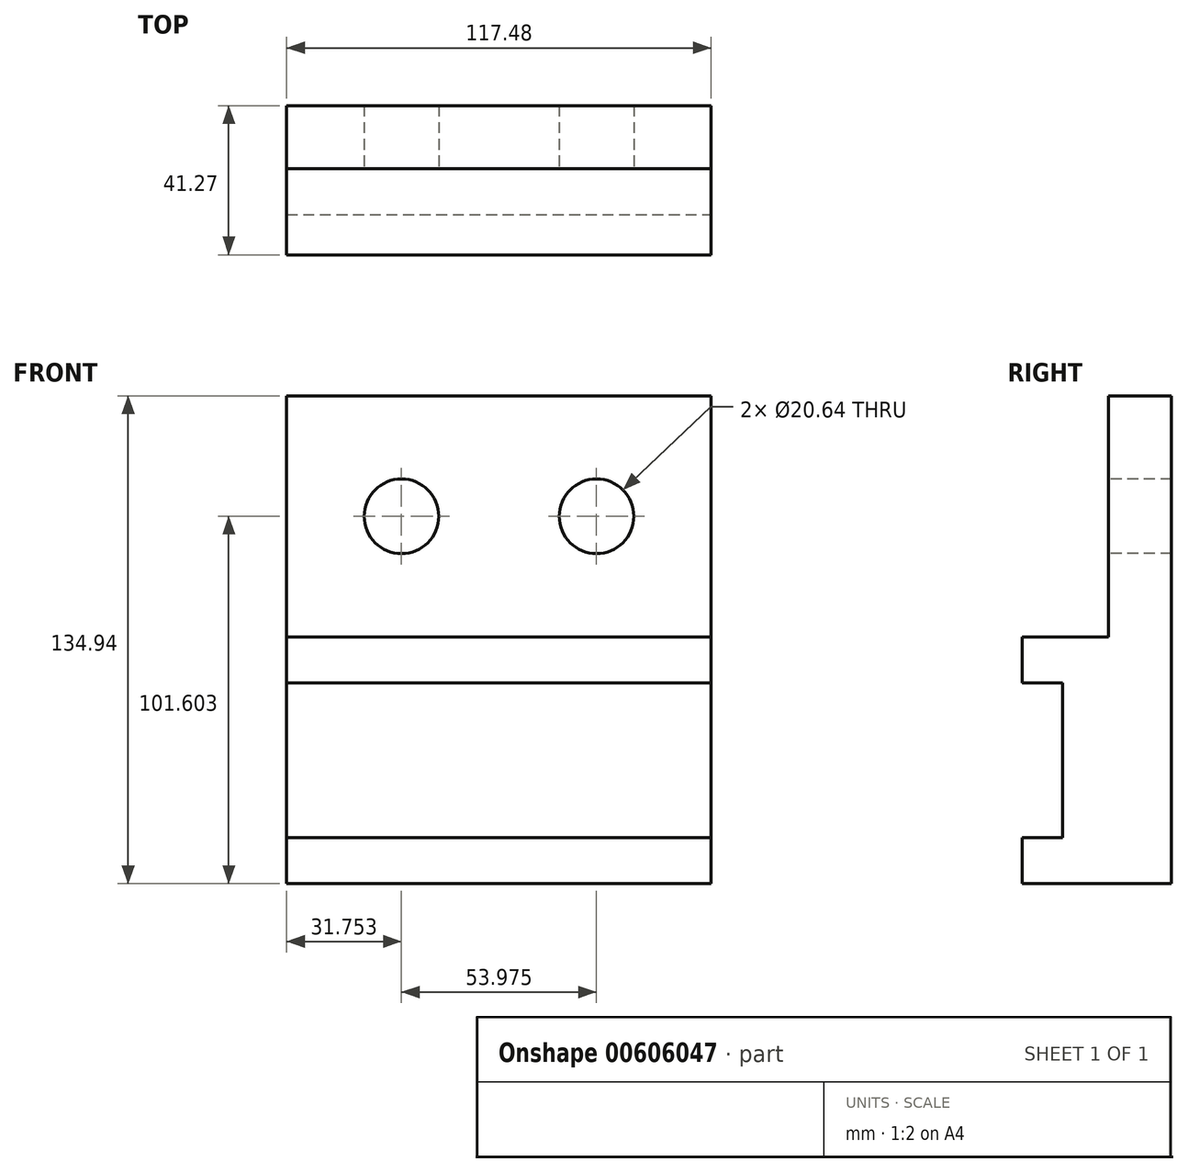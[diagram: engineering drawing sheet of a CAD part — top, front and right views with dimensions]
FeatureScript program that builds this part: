
annotation { "Feature Type Name" : "Feature", "Feature Type Description" : "" }
export const myFeature = defineFeature(function(context is Context, id is Id, definition is map)
    precondition{}
    {
        {
            var Q0;
            Q0=qCreatedBy(makeId("Front.planeOp"),FACE);
            var sketch = newSketch(context, id + "F0", { "sketchPlane" : qUnion([Q0])});
            skLineSegment(sketch, "E0.bottom", {"start": v(-57.2, 10.6) * mm, "end": v(60.27, 10.6) * mm});
            skLineSegment(sketch, "E0.top", {"start": v(-57.2, -57.67) * mm, "end": v(60.27, -57.67) * mm});
            skLineSegment(sketch, "E0.left", {"start": v(-57.2, 10.6) * mm, "end": v(-57.2, -57.67) * mm});
            skLineSegment(sketch, "E0.right", {"start": v(60.27, 10.6) * mm, "end": v(60.27, -57.67) * mm});
            skSolve(sketch);
        }
        {
            var Q0;
            Q0=makeQuery(id+"F0.imprint","IMPRINT",FACE,{"disambiguationData":[TD([[makeQuery(id+"F0.imprint","IMPRINT",EDGE,{"derivedFrom":sQuery(id+"F0.wireOp",EDGE,"E0.bottom")}),-1.0]])]});
            extrude(context, id + "F1", {"entities" : qUnion([Q0]), "depth" : 41.27 * mm, "offsetDistance" : 25.4 * mm});
        }
        {
            var Q0;
            Q0=makeQuery(id+"F1.opExtrude","CAP_FACE",FACE,{"disambiguationData":[OSD([sQuery(id+"F0.wireOp",EDGE,"E0.bottom"),sQuery(id+"F0.wireOp",EDGE,"E0.top"),sQuery(id+"F0.wireOp",EDGE,"E0.left"),sQuery(id+"F0.wireOp",EDGE,"E0.right")])],"isStart":false});
            var sketch = newSketch(context, id + "F2", { "sketchPlane" : qUnion([Q0])});
            skLineSegment(sketch, "E1.bottom", {"start": v(-57.2, -2.1) * mm, "end": v(60.27, -2.1) * mm});
            skLineSegment(sketch, "E1.top", {"start": v(-57.2, -44.97) * mm, "end": v(60.27, -44.97) * mm});
            skLineSegment(sketch, "E1.left", {"start": v(-57.2, -2.1) * mm, "end": v(-57.2, -44.97) * mm});
            skLineSegment(sketch, "E1.right", {"start": v(60.27, -2.1) * mm, "end": v(60.27, -44.97) * mm});
            skSolve(sketch);
        }
        {
            var Q0;
            Q0=makeQuery(id+"F2.imprint","IMPRINT",FACE,{"disambiguationData":[TD([[makeQuery(id+"F2.imprint","IMPRINT",EDGE,{"derivedFrom":sQuery(id+"F2.wireOp",EDGE,"E1.bottom")}),-1.0]])]});
            extrude(context, id + "F3", {"entities" : qUnion([Q0]), "operationType" : NewBodyOperationType.REMOVE, "oppositeDirection" : true, "depth" : 11.1 * mm, "offsetDistance" : 25.4 * mm});
        }
        {
            var Q0;
            Q0=makeQuery(id+"F1.opExtrude","SWEPT_FACE",FACE,{"disambiguationData":[OSD([sQuery(id+"F0.wireOp",EDGE,"E0.bottom")])]});
            var sketch = newSketch(context, id + "F4", { "sketchPlane" : qUnion([Q0])});
            skLineSegment(sketch, "E2.bottom", {"start": v(-57.2, 0) * mm, "end": v(60.27, 0) * mm});
            skLineSegment(sketch, "E2.top", {"start": v(-57.2, -17.46) * mm, "end": v(60.27, -17.46) * mm});
            skLineSegment(sketch, "E2.left", {"start": v(-57.2, 0) * mm, "end": v(-57.2, -17.46) * mm});
            skLineSegment(sketch, "E2.right", {"start": v(60.27, 0) * mm, "end": v(60.27, -17.46) * mm});
            skSolve(sketch);
        }
        {
            var Q0;
            Q0=makeQuery(id+"F4.imprint","IMPRINT",FACE,{"disambiguationData":[TD([[makeQuery(id+"F4.imprint","IMPRINT",EDGE,{"derivedFrom":sQuery(id+"F4.wireOp",EDGE,"E2.bottom")}),-1.0]])]});
            extrude(context, id + "F5", {"entities" : qUnion([Q0]), "operationType" : NewBodyOperationType.ADD, "depth" : 66.67 * mm, "offsetDistance" : 25.4 * mm});
        }
        {
            var Q0;
            Q0=makeQuery(id+"F5.opExtrude","SWEPT_FACE",FACE,{"disambiguationData":[OSD([sQuery(id+"F4.wireOp",EDGE,"E2.top")])]});
            var sketch = newSketch(context, id + "F6", { "sketchPlane" : qUnion([Q0])});
            skCircle(sketch, "E3", {"center": v(-25.46, 43.93) * mm, "radius": 10.32 * mm});
            skPoint(sketch, "E3.centerSnap0", {"position": v(-57.2, 43.93) * mm});
            skCircle(sketch, "E4", {"center": v(28.52, 43.93) * mm, "radius": 10.32 * mm});
            skPoint(sketch, "E4.centerSnap0", {"position": v(60.27, 43.93) * mm});
            skSolve(sketch);
        }
        {
            var Q0;
            Q0=makeQuery(id+"F6.imprint","IMPRINT",FACE,{"disambiguationData":[TD([[makeQuery(id+"F6.imprint","IMPRINT",EDGE,{"derivedFrom":sQuery(id+"F6.wireOp",EDGE,"E4")}),1.0]])]});
            var Q1;
            Q1=makeQuery(id+"F6.imprint","IMPRINT",FACE,{"disambiguationData":[TD([[makeQuery(id+"F6.imprint","IMPRINT",EDGE,{"derivedFrom":sQuery(id+"F6.wireOp",EDGE,"E3")}),1.0]])]});
            extrude(context, id + "F7", {"entities" : qUnion([Q0, Q1]), "operationType" : NewBodyOperationType.REMOVE, "oppositeDirection" : true, "depth" : 101.6 * mm, "offsetDistance" : 25.4 * mm});
        }
    });
